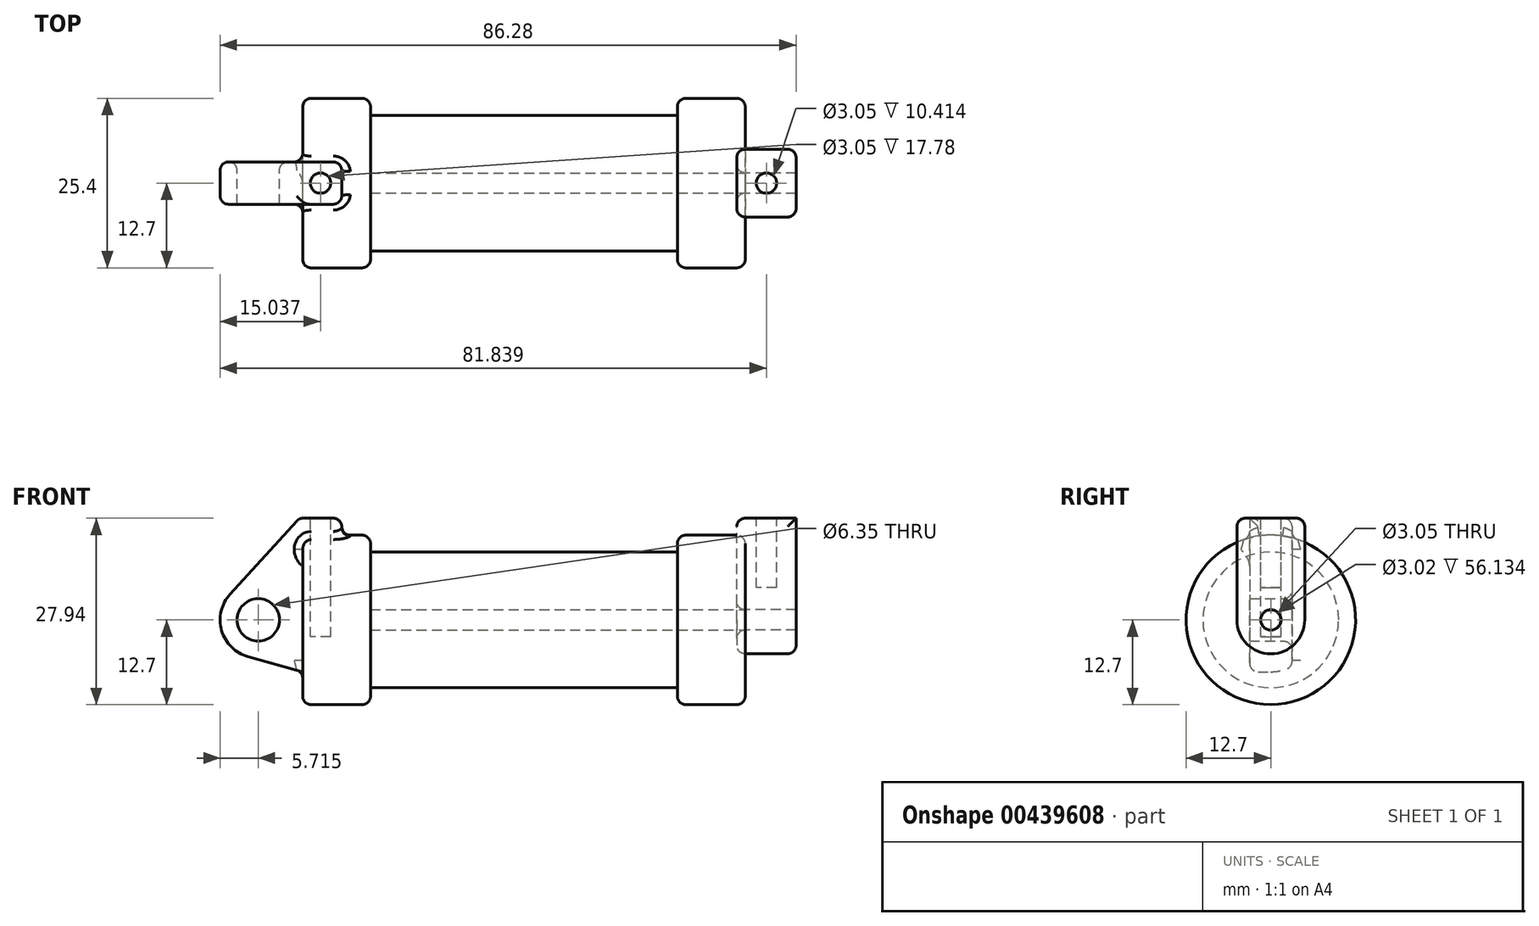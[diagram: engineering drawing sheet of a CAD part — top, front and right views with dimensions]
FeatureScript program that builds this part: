
annotation { "Feature Type Name" : "Feature", "Feature Type Description" : "" }
export const myFeature = defineFeature(function(context is Context, id is Id, definition is map)
    precondition{}
    {
        {
            var Q0;
            Q0=qCreatedBy(makeId("Front.planeOp"),FACE);
            var sketch = newSketch(context, id + "F0", { "sketchPlane" : qUnion([Q0])});
            skLineSegment(sketch, "E0", {"start": v(0, 0) * mm, "end": v(0, 12.7) * mm});
            skLineSegment(sketch, "E1", {"start": v(0, 12.7) * mm, "end": v(10.16, 12.7) * mm});
            skLineSegment(sketch, "E2", {"start": v(10.16, 12.7) * mm, "end": v(10.16, 10.16) * mm});
            skLineSegment(sketch, "E3", {"start": v(10.16, 10.16) * mm, "end": v(56.13, 10.16) * mm});
            skLineSegment(sketch, "E4", {"start": v(56.13, 10.16) * mm, "end": v(56.13, 12.7) * mm});
            skLineSegment(sketch, "E5", {"start": v(56.13, 12.7) * mm, "end": v(66.3, 12.7) * mm});
            skLineSegment(sketch, "E6", {"start": v(66.3, 12.7) * mm, "end": v(66.3, 0) * mm});
            skLineSegment(sketch, "E7", {"start": v(66.3, 0) * mm, "end": v(0, 0) * mm});
            skLineSegment(sketch, "E8", {"start": v(5.84, 15.24) * mm, "end": v(-0.5, 15.24) * mm});
            skLineSegment(sketch, "E9", {"start": v(-0.5, 15.24) * mm, "end": v(-10.88, 3.85) * mm});
            skLineSegment(sketch, "E10", {"start": v(0, 0) * mm, "end": v(-6.65, 0) * mm});
            skCircle(sketch, "E11", {"center": v(-6.65, 0) * mm, "radius": 5.72 * mm});
            skCircle(sketch, "E12", {"center": v(-6.65, 0) * mm, "radius": 3.18 * mm});
            skLineSegment(sketch, "E13", {"start": v(5.84, 15.24) * mm, "end": v(5.84, -9.4) * mm});
            skLineSegment(sketch, "E14", {"start": v(5.84, -9.4) * mm, "end": v(-8.18, -5.5) * mm});
            skSolve(sketch);
        }
        {
            var Q0;
            {var subQ0=sQuery(id+"F0.wireOp",EDGE,"E2");Q0=makeQuery(id+"F0.imprint","IMPRINT",FACE,{"disambiguationData":[TD([[makeQuery(id+"F0.imprint","IMPRINT",EDGE,{"derivedFrom":subQ0}),-1.0]])]});}
            var Q1;
            {var subQ0=sQuery(id+"F0.wireOp",EDGE,"E0");Q1=makeQuery(id+"F0.imprint","IMPRINT",FACE,{"disambiguationData":[TD([[makeQuery(id+"F0.imprint","IMPRINT",EDGE,{"derivedFrom":subQ0}),-1.0]])]});}
            var Q2;
            Q2=sQuery(id+"F0.wireOp",EDGE,"E10");
            revolve(context, id + "F1", {"entities" : qUnion([Q0, Q1]), "axis" : qUnion([Q2]), "revolveType" : RevolveType.FULL});
        }
        {
            var Q0;
            {var subQ1=sQuery(id+"F0.wireOp",EDGE,"E0");Q0=makeQuery(id+"F0.imprint","IMPRINT",FACE,{"disambiguationData":[TD([[makeQuery(id+"F0.imprint","IMPRINT",EDGE,{"derivedFrom":subQ1}),1.0]])]});}
            var Q1;
            {var subQ0=sQuery(id+"F0.wireOp",EDGE,"E0");Q1=makeQuery(id+"F0.imprint","IMPRINT",FACE,{"disambiguationData":[TD([[makeQuery(id+"F0.imprint","IMPRINT",EDGE,{"derivedFrom":subQ0}),-1.0]])]});}
            var Q2;
            {var subQ0=sQuery(id+"F0.wireOp",EDGE,"E14");Q2=makeQuery(id+"F0.imprint","IMPRINT",FACE,{"disambiguationData":[TD([[makeQuery(id+"F0.imprint","IMPRINT",EDGE,{"derivedFrom":subQ0}),-1.0]])]});}
            var Q3;
            {var subQ5=sQuery(id+"F0.wireOp",EDGE,"E12");Q3=makeQuery(id+"F0.imprint","IMPRINT",FACE,{"disambiguationData":[TD([[makeQuery(id+"F0.imprint","IMPRINT",EDGE,{"derivedFrom":subQ5}),-1.0]])]});}
            extrude(context, id + "F2", {"entities" : qUnion([Q0, Q1, Q2, Q3]), "operationType" : NewBodyOperationType.ADD, "endBound" : BoundingType.SYMMETRIC, "depth" : 6.35 * mm});
        }
        {
            var Q0;
            Q0=makeQuery(id+"F1.opRevolve","SWEPT_FACE",FACE,{"disambiguationData":[OSD([sQuery(id+"F0.wireOp",EDGE,"E6")])]});
            var sketch = newSketch(context, id + "F3", { "sketchPlane" : qUnion([Q0])});
            skCircle(sketch, "E15", {"center": v(0, 0) * mm, "radius": 1.52 * mm});
            skCircle(sketch, "E16", {"center": v(0, 0) * mm, "radius": 5.08 * mm});
            skLineSegment(sketch, "E17", {"start": v(0, 0) * mm, "end": v(-5.08, 0) * mm, "construction": true});
            skLineSegment(sketch, "E18", {"start": v(-5.08, 0) * mm, "end": v(5.08, 0) * mm, "construction": true});
            skLineSegment(sketch, "E19", {"start": v(5.08, 0) * mm, "end": v(5.08, 15.24) * mm});
            skLineSegment(sketch, "E20", {"start": v(-5.08, 0) * mm, "end": v(-5.08, 15.24) * mm});
            skLineSegment(sketch, "E21", {"start": v(-5.08, 15.24) * mm, "end": v(5.08, 15.24) * mm});
            skSolve(sketch);
        }
        {
            var Q0;
            Q0 = qSketchRegion(id + "F3", true);
            extrude(context, id + "F4", {"entities" : qUnion([Q0]), "depth" : 7.62 * mm, "hasSecondDirection" : true, "secondDirectionOppositeDirection" : true, "secondDirectionDepth" : 1.27 * mm});
        }
        {
            var Q0;
            Q0=makeQuery(id+"F1.opRevolve","SWEPT_FACE",FACE,{"disambiguationData":[OSD([sQuery(id+"F0.wireOp",EDGE,"E6")])]});
            var sketch = newSketch(context, id + "F5", { "sketchPlane" : qUnion([Q0])});
            skCircle(sketch, "E22", {"center": v(0, 0) * mm, "radius": 1.51 * mm});
            skSolve(sketch);
        }
        {
            var Q0;
            Q0=makeQuery(id+"F4.opExtrude","SWEPT_FACE",FACE,{"disambiguationData":[OSD([sQuery(id+"F3.wireOp",EDGE,"E21")])]});
            var sketch = newSketch(context, id + "F6", { "sketchPlane" : qUnion([Q0])});
            skLineSegment(sketch, "E23", {"start": v(65.02, 0) * mm, "end": v(73.91, 0) * mm, "construction": true});
            skLineSegment(sketch, "E24", {"start": v(69.47, 5.08) * mm, "end": v(69.47, -5.08) * mm, "construction": true});
            skCircle(sketch, "E25", {"center": v(69.47, 0) * mm, "radius": 1.52 * mm});
            skSolve(sketch);
        }
        {
            var Q0;
            Q0=makeQuery(id+"F2.opExtrude","SWEPT_FACE",FACE,{"disambiguationData":[OSD([sQuery(id+"F0.wireOp",EDGE,"E8")])]});
            var sketch = newSketch(context, id + "F7", { "sketchPlane" : qUnion([Q0])});
            skLineSegment(sketch, "E26", {"start": v(2.67, -3.18) * mm, "end": v(2.67, 3.18) * mm, "construction": true});
            skLineSegment(sketch, "E27", {"start": v(-0.5, 0) * mm, "end": v(5.84, 0) * mm, "construction": true});
            skCircle(sketch, "E28", {"center": v(2.67, 0) * mm, "radius": 1.52 * mm});
            skSolve(sketch);
        }
        {
            var Q0;
            Q0=makeQuery(id+"F5.imprint","IMPRINT",FACE,{"disambiguationData":[TD([[makeQuery(id+"F5.imprint","IMPRINT",EDGE,{"derivedFrom":sQuery(id+"F5.wireOp",EDGE,"E22")}),1.0]])]});
            var Q1;
            Q1=makeQuery(id+"F1.opRevolve","SWEPT_FACE",FACE,{"disambiguationData":[OSD([sQuery(id+"F0.wireOp",EDGE,"E2")])]});
            extrude(context, id + "F8", {"entities" : qUnion([Q0]), "operationType" : NewBodyOperationType.REMOVE, "endBound" : BoundingType.UP_TO_SURFACE, "oppositeDirection" : true, "endBoundEntityFace" : qUnion([Q1]), "depth" : 25.4 * mm});
        }
        {
            var Q0;
            Q0=makeQuery(id+"F7.imprint","IMPRINT",FACE,{"disambiguationData":[TD([[makeQuery(id+"F7.imprint","IMPRINT",EDGE,{"derivedFrom":sQuery(id+"F7.wireOp",EDGE,"E28")}),1.0]])]});
            var Q1;
            Q1=sQuery(id+"F7.wireOp",EDGE,"E28");
            extrude(context, id + "F9", {"entities" : qUnion([Q0]), "operationType" : NewBodyOperationType.REMOVE, "surfaceEntities" : qUnion([Q1]), "oppositeDirection" : true, "depth" : 17.78 * mm});
        }
        {
            var Q0;
            Q0=makeQuery(id+"F6.imprint","IMPRINT",FACE,{"disambiguationData":[TD([[makeQuery(id+"F6.imprint","IMPRINT",EDGE,{"derivedFrom":sQuery(id+"F6.wireOp",EDGE,"E25")}),1.0]])]});
            extrude(context, id + "F10", {"entities" : qUnion([Q0]), "operationType" : NewBodyOperationType.REMOVE, "oppositeDirection" : true, "depth" : 10.4 * mm});
        }
        {
            var Q0;
            Q0=makeQuery(id+"F1.opRevolve","SWEPT_FACE",FACE,{"disambiguationData":[OSD([sQuery(id+"F0.wireOp",EDGE,"E5")])]});
            var Q1;
            Q1=makeQuery(id+"F4.opExtrude","SWEPT_FACE",FACE,{"disambiguationData":[OSD([sQuery(id+"F3.wireOp",EDGE,"E20")])]});
            var Q2;
            Q2=makeQuery(id+"F4.opExtrude","SWEPT_FACE",FACE,{"disambiguationData":[OSD([sQuery(id+"F3.wireOp",EDGE,"E16")])]});
            var Q3;
            Q3=makeQuery(id+"F4.opExtrude","SWEPT_FACE",FACE,{"disambiguationData":[OSD([sQuery(id+"F3.wireOp",EDGE,"E19")])]});
            var Q4;
            Q4=makeQuery(id+"F4.opExtrude","CAP_FACE",FACE,{"disambiguationData":[OSD([sQuery(id+"F3.wireOp",EDGE,"E15"),sQuery(id+"F3.wireOp",EDGE,"E16"),sQuery(id+"F3.wireOp",EDGE,"E19"),sQuery(id+"F3.wireOp",EDGE,"E20"),sQuery(id+"F3.wireOp",EDGE,"E21")])],"isStart":true});
            fillet(context, id + "F11", {"entities" : qUnion([Q0, Q1, Q2, Q3, Q4]), "radius" : 1.27 * mm, "tangentPropagation" : true, "allowEdgeOverflow" : false});
        }
        {
            var Q0;
            Q0=makeQuery(id+"F1.opRevolve","SWEPT_FACE",FACE,{"disambiguationData":[OSD([sQuery(id+"F0.wireOp",EDGE,"E1")])]});
            var Q1;
            Q1=makeQuery(id+"F1.opRevolve","SWEPT_EDGE",EDGE,{"disambiguationData":[OSD([sQuery(id+"F0.wireOp",EDGE,"E1"),sQuery(id+"F0.wireOp",EDGE,"E2")])]});
            var Q2;
            Q2=makeQuery(id+"F2.opExtrude","SWEPT_FACE",FACE,{"disambiguationData":[OSD([sQuery(id+"F0.wireOp",EDGE,"E9")])]});
            var Q3;
            Q3=makeQuery(id+"F2.opExtrude","SWEPT_FACE",FACE,{"disambiguationData":[OSD([sQuery(id+"F0.wireOp",EDGE,"E11")])]});
            var Q4;
            Q4=makeQuery(id+"F2.opExtrude","CAP_FACE",FACE,{"disambiguationData":[OSD([sQuery(id+"F0.wireOp",EDGE,"E8"),sQuery(id+"F0.wireOp",EDGE,"E9"),sQuery(id+"F0.wireOp",EDGE,"E11"),sQuery(id+"F0.wireOp",EDGE,"E12"),sQuery(id+"F0.wireOp",EDGE,"E13"),sQuery(id+"F0.wireOp",EDGE,"E14")])],"isStart":true});
            var Q5;
            Q5=makeQuery(id+"F2.opExtrude","SWEPT_FACE",FACE,{"disambiguationData":[OSD([sQuery(id+"F0.wireOp",EDGE,"E13")])]});
            fillet(context, id + "F12", {"entities" : qUnion([Q0, Q1, Q2, Q3, Q4, Q5]), "radius" : 1.27 * mm, "tangentPropagation" : true, "allowEdgeOverflow" : false});
        }
    });
